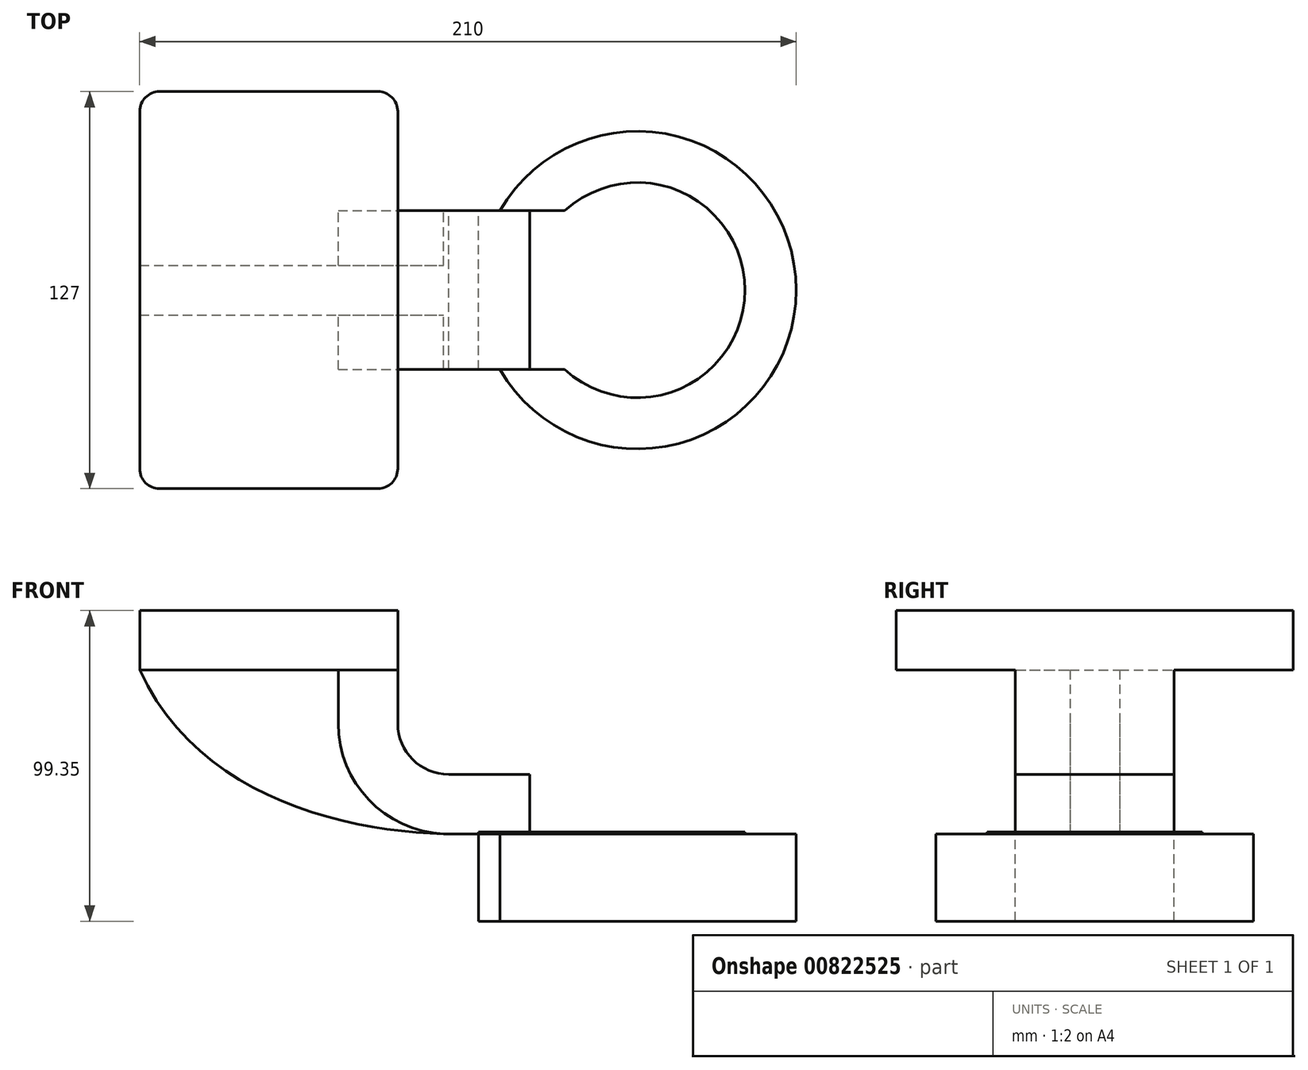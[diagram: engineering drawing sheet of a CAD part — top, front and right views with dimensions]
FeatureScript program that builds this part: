
annotation { "Feature Type Name" : "Feature", "Feature Type Description" : "" }
export const myFeature = defineFeature(function(context is Context, id is Id, definition is map)
    precondition{}
    {
        {
            var Q0;
            Q0=qCreatedBy(makeId("Front.planeOp"),FACE);
            var sketch = newSketch(context, id + "F0", { "sketchPlane" : qUnion([Q0])});
            skLineSegment(sketch, "E0.bottom", {"start": v(-41.28, 9.52) * mm, "end": v(41.28, 9.52) * mm});
            skLineSegment(sketch, "E0.top", {"start": v(-41.28, -9.52) * mm, "end": v(41.28, -9.52) * mm});
            skLineSegment(sketch, "E0.left", {"start": v(-41.28, 9.52) * mm, "end": v(-41.28, -9.52) * mm});
            skLineSegment(sketch, "E0.right", {"start": v(41.28, 9.52) * mm, "end": v(41.28, -9.52) * mm});
            skPoint(sketch, "E0.middle", {"position": v(0, 0) * mm});
            skLineSegment(sketch, "E1.bottom", {"start": v(67.12, -89.82) * mm, "end": v(117.92, -89.82) * mm});
            skLineSegment(sketch, "E1.top", {"start": v(67.12, -61.24) * mm, "end": v(117.92, -61.24) * mm});
            skLineSegment(sketch, "E1.left", {"start": v(67.12, -89.82) * mm, "end": v(67.12, -61.24) * mm});
            skLineSegment(sketch, "E1.right", {"start": v(117.92, -89.82) * mm, "end": v(117.92, -61.24) * mm});
            skPoint(sketch, "E1.middle", {"position": v(92.52, -75.53) * mm});
            skLineSegment(sketch, "E2", {"start": v(41.28, -9.52) * mm, "end": v(41.28, -26.58) * mm});
            skArc(sketch, "E3", {"start": v(41.28, -26.58) * mm, "mid": v(46.05, -38.1) * mm, "end": v(57.57, -42.88) * mm});
            skLineSegment(sketch, "E4", {"start": v(57.57, -42.88) * mm, "end": v(83.52, -42.88) * mm});
            skLineSegment(sketch, "E5.0", {"start": v(57.57, -61.93) * mm, "end": v(83.52, -61.93) * mm});
            skArc(sketch, "E5.1", {"start": v(22.23, -26.58) * mm, "mid": v(32.58, -51.57) * mm, "end": v(57.57, -61.93) * mm});
            skLineSegment(sketch, "E5.2", {"start": v(22.22, -9.53) * mm, "end": v(22.22, -26.58) * mm});
            skLineSegment(sketch, "E6", {"start": v(83.52, -42.88) * mm, "end": v(83.52, -61.93) * mm});
            skFitSpline(sketch, "E7", {"points": [v(-41.28, -9.52) * mm, v(57.57, -61.93) * mm], "startDerivative": vector(56.25, -122.12) * mm, "endDerivative": vector(98.86, -1.75) * mm});
            skSolve(sketch);
        }
        {
            var Q0;
            Q0=makeQuery(id+"F0.imprint","IMPRINT",FACE,{"disambiguationData":[TD([[makeQuery(id+"F0.imprint","IMPRINT",EDGE,{"derivedFrom":sQuery(id+"F0.wireOp",EDGE,"E0.bottom")}),-1.0]])]});
            extrude(context, id + "F1", {"entities" : qUnion([Q0]), "endBound" : BoundingType.SYMMETRIC, "depth" : 127 * mm, "offsetDistance" : 25.4 * mm});
        }
        {
            var Q0;
            {var subQ12=sQuery(id+"F0.wireOp",EDGE,"E2");Q0=makeQuery(id+"F0.imprint","IMPRINT",FACE,{"disambiguationData":[TD([[makeQuery(id+"F0.imprint","IMPRINT",EDGE,{"derivedFrom":subQ12}),-1.0]])]});}
            var Q1;
            {var subQ1=sQuery(id+"F0.wireOp",EDGE,"E1.bottom");Q1=makeQuery(id+"F0.imprint","IMPRINT",FACE,{"disambiguationData":[TD([[makeQuery(id+"F0.imprint","IMPRINT",EDGE,{"derivedFrom":subQ1}),1.0]])]});}
            extrude(context, id + "F2", {"entities" : qUnion([Q0, Q1]), "operationType" : NewBodyOperationType.ADD, "endBound" : BoundingType.SYMMETRIC, "depth" : 50.8 * mm, "offsetDistance" : 25.4 * mm});
        }
        {
            var Q0;
            {var subQ3=sQuery(id+"F0.wireOp",EDGE,"E5.2");Q0=makeQuery(id+"F0.imprint","IMPRINT",FACE,{"disambiguationData":[TD([[makeQuery(id+"F0.imprint","IMPRINT",EDGE,{"derivedFrom":subQ3}),-1.0]])]});}
            extrude(context, id + "F3", {"entities" : qUnion([Q0]), "operationType" : NewBodyOperationType.ADD, "endBound" : BoundingType.SYMMETRIC, "depth" : 15.88 * mm, "offsetDistance" : 25.4 * mm});
        }
        {
            var Q0;
            {var subQ1=sQuery(id+"F0.wireOp",EDGE,"E1.bottom");Q0=makeQuery(id+"F0.imprint","IMPRINT",FACE,{"disambiguationData":[TD([[makeQuery(id+"F0.imprint","IMPRINT",EDGE,{"derivedFrom":subQ1}),1.0]])]});}
            var Q1;
            Q1=sQuery(id+"F0.wireOp",EDGE,"E1.right");
            revolve(context, id + "F4", {"operationType" : NewBodyOperationType.ADD, "surfaceOperationType" : NewSurfaceOperationType.NEW, "entities" : qUnion([Q0]), "axis" : qUnion([Q1]), "revolveType" : RevolveType.FULL});
        }
        {
            var Q0;
            Q0=makeQuery(id+"F1.opExtrude","CAP_EDGE",EDGE,{"disambiguationData":[OSD([sQuery(id+"F0.wireOp",EDGE,"E0.right")])],"isStart":true});
            var Q1;
            Q1=makeQuery(id+"F1.opExtrude","CAP_EDGE",EDGE,{"disambiguationData":[OSD([sQuery(id+"F0.wireOp",EDGE,"E0.right")])],"isStart":false});
            var Q2;
            Q2=makeQuery(id+"F1.opExtrude","CAP_EDGE",EDGE,{"disambiguationData":[OSD([sQuery(id+"F0.wireOp",EDGE,"E0.left")])],"isStart":false});
            fillet(context, id + "F5", {"entities" : qUnion([Q0, Q1, Q2]), "radius" : 6.35 * mm, "tangentPropagation" : true, "allowEdgeOverflow" : false});
        }
        {
            var Q0;
            Q0=makeQuery(id+"F1.opExtrude","CAP_EDGE",EDGE,{"disambiguationData":[OSD([sQuery(id+"F0.wireOp",EDGE,"E0.left")])],"isStart":true});
            fillet(context, id + "F6", {"entities" : qUnion([Q0]), "radius" : 6.35 * mm, "tangentPropagation" : true, "allowEdgeOverflow" : false});
        }
    });
